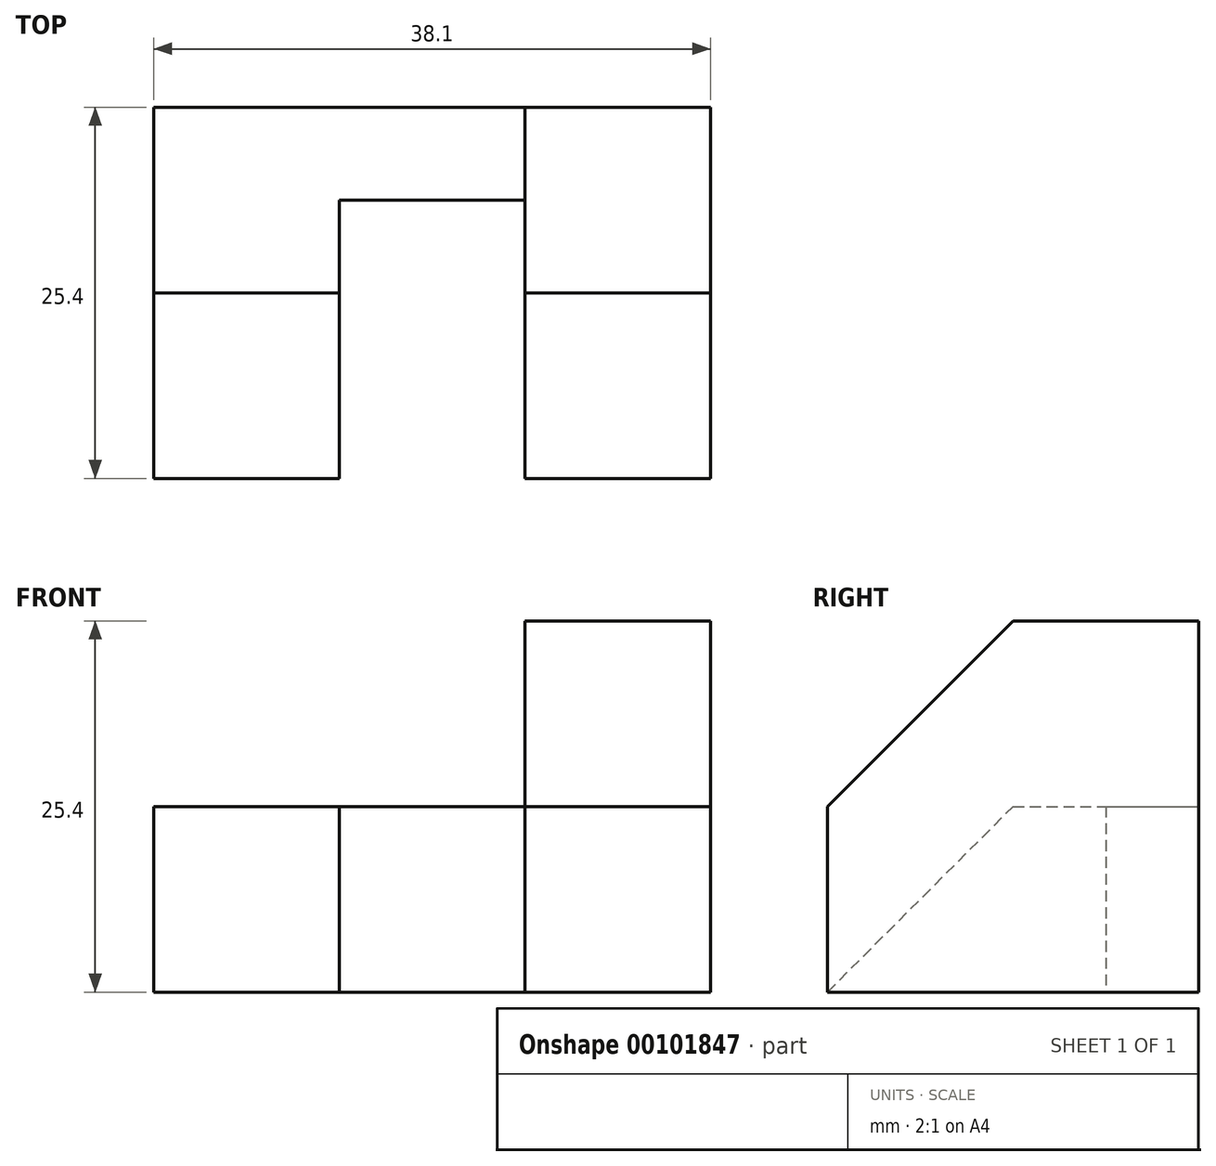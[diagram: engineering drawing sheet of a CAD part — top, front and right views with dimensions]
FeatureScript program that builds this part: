
annotation { "Feature Type Name" : "Feature", "Feature Type Description" : "" }
export const myFeature = defineFeature(function(context is Context, id is Id, definition is map)
    precondition{}
    {
        {
            var Q0;
            Q0=qCreatedBy(makeId("Right.planeOp"),FACE);
            var sketch = newSketch(context, id + "F0", { "sketchPlane" : qUnion([Q0])});
            skLineSegment(sketch, "E0", {"start": v(0, 0) * mm, "end": v(25.4, 0) * mm});
            skLineSegment(sketch, "E1", {"start": v(25.4, 0) * mm, "end": v(25.4, 25.4) * mm});
            skLineSegment(sketch, "E2", {"start": v(0, 25.4) * mm, "end": v(25.4, 25.4) * mm});
            skLineSegment(sketch, "E3", {"start": v(0, 0) * mm, "end": v(0, 25.4) * mm});
            skSolve(sketch);
        }
        {
            var Q0;
            Q0 = qSketchRegion(id + "F0", true);
            extrude(context, id + "F1", {"entities" : qUnion([Q0]), "oppositeDirection" : true, "depth" : 38.1 * mm});
        }
        {
            var Q0;
            Q0=makeQuery(id+"F1.opExtrude","SWEPT_FACE",FACE,{"disambiguationData":[OSD([sQuery(id+"F0.wireOp",EDGE,"E0")])]});
            var sketch = newSketch(context, id + "F2", { "sketchPlane" : qUnion([Q0])});
            skLineSegment(sketch, "E4.bottom", {"start": v(-25.4, 0) * mm, "end": v(-12.7, 0) * mm});
            skLineSegment(sketch, "E4.top", {"start": v(-25.4, -19.05) * mm, "end": v(-12.7, -19.05) * mm});
            skLineSegment(sketch, "E4.left", {"start": v(-25.4, 0) * mm, "end": v(-25.4, -19.05) * mm});
            skLineSegment(sketch, "E4.right", {"start": v(-12.7, 0) * mm, "end": v(-12.7, -19.05) * mm});
            skSolve(sketch);
        }
        {
            var Q0;
            Q0 = qSketchRegion(id + "F2", true);
            extrude(context, id + "F3", {"entities" : qUnion([Q0]), "operationType" : NewBodyOperationType.REMOVE, "endBound" : BoundingType.THROUGH_ALL, "oppositeDirection" : true, "depth" : 25.4 * mm});
        }
        {
            var Q0;
            Q0=makeQuery(id+"F1.opExtrude","CAP_FACE",FACE,{"disambiguationData":[OSD([sQuery(id+"F0.wireOp",EDGE,"E0"),sQuery(id+"F0.wireOp",EDGE,"E1"),sQuery(id+"F0.wireOp",EDGE,"E2"),sQuery(id+"F0.wireOp",EDGE,"E3")])],"isStart":true});
            var sketch = newSketch(context, id + "F4", { "sketchPlane" : qUnion([Q0])});
            skLineSegment(sketch, "E5", {"start": v(0, 12.7) * mm, "end": v(12.7, 25.4) * mm});
            skSolve(sketch);
        }
        {
            var Q0;
            {var subQ0=sQuery(id+"F4.wireOp",EDGE,"E5");Q0=makeQuery(id+"F4.imprint","IMPRINT",FACE,{"disambiguationData":[TD([[makeQuery(id+"F4.imprint","IMPRINT",EDGE,{"derivedFrom":subQ0}),1.0]])]});}
            extrude(context, id + "F5", {"entities" : qUnion([Q0]), "operationType" : NewBodyOperationType.REMOVE, "endBound" : BoundingType.THROUGH_ALL, "oppositeDirection" : true, "depth" : 12.7 * mm});
        }
        {
            var Q0;
            Q0=makeQuery(id+"F1.opExtrude","SWEPT_FACE",FACE,{"disambiguationData":[OSD([sQuery(id+"F0.wireOp",EDGE,"E1")])]});
            var sketch = newSketch(context, id + "F6", { "sketchPlane" : qUnion([Q0])});
            skLineSegment(sketch, "E6", {"start": v(38.1, 12.7) * mm, "end": v(12.7, 12.7) * mm});
            skLineSegment(sketch, "E7", {"start": v(12.7, 12.7) * mm, "end": v(12.7, 25.4) * mm});
            skLineSegment(sketch, "E8", {"start": v(12.7, 25.4) * mm, "end": v(38.1, 25.4) * mm});
            skLineSegment(sketch, "E9", {"start": v(38.1, 25.4) * mm, "end": v(38.1, 12.7) * mm});
            skSolve(sketch);
        }
        {
            var Q0;
            Q0=makeQuery(id+"F6.imprint","IMPRINT",FACE,{"disambiguationData":[TD([[makeQuery(id+"F6.imprint","IMPRINT",EDGE,{"derivedFrom":sQuery(id+"F6.wireOp",EDGE,"E6")}),-1.0]])]});
            extrude(context, id + "F7", {"entities" : qUnion([Q0]), "operationType" : NewBodyOperationType.REMOVE, "endBound" : BoundingType.THROUGH_ALL, "oppositeDirection" : true, "depth" : 25.4 * mm});
        }
        {
            var Q0;
            Q0=makeQuery(id+"F1.opExtrude","CAP_FACE",FACE,{"disambiguationData":[OSD([sQuery(id+"F0.wireOp",EDGE,"E0"),sQuery(id+"F0.wireOp",EDGE,"E1"),sQuery(id+"F0.wireOp",EDGE,"E2"),sQuery(id+"F0.wireOp",EDGE,"E3")])],"isStart":false});
            var sketch = newSketch(context, id + "F8", { "sketchPlane" : qUnion([Q0])});
            skLineSegment(sketch, "E10", {"start": v(0, 0) * mm, "end": v(-12.7, 12.7) * mm});
            skSolve(sketch);
        }
        {
            var Q0;
            {var subQ0=sQuery(id+"F8.wireOp",EDGE,"E10");Q0=makeQuery(id+"F8.imprint","IMPRINT",FACE,{"disambiguationData":[TD([[makeQuery(id+"F8.imprint","IMPRINT",EDGE,{"derivedFrom":subQ0}),-1.0]])]});}
            extrude(context, id + "F9", {"entities" : qUnion([Q0]), "operationType" : NewBodyOperationType.REMOVE, "oppositeDirection" : true, "depth" : 12.7 * mm});
        }
    });
